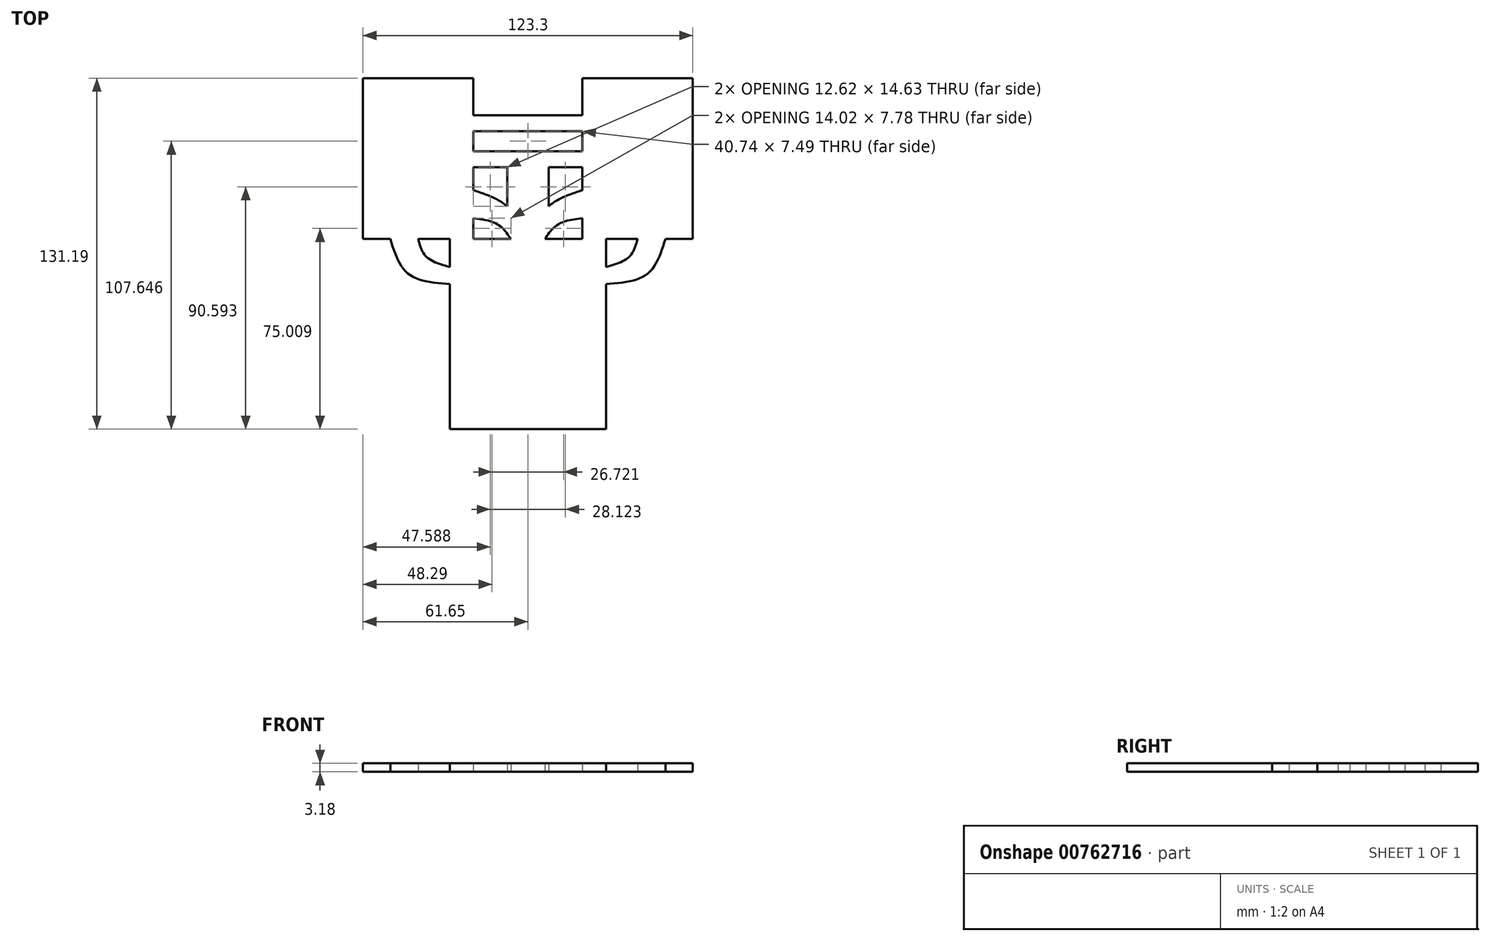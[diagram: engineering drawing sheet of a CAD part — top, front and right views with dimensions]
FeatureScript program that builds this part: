
annotation { "Feature Type Name" : "Feature", "Feature Type Description" : "" }
export const myFeature = defineFeature(function(context is Context, id is Id, definition is map)
    precondition{}
    {
        {
            var Q0;
            Q0=qCreatedBy(makeId("Top.planeOp"),FACE);
            var sketch = newSketch(context, id + "F0", { "sketchPlane" : qUnion([Q0])});
            skLineSegment(sketch, "E0", {"start": v(0, 2.42) * mm, "end": v(29.21, 2.42) * mm});
            skLineSegment(sketch, "E1", {"start": v(0, 2.42) * mm, "end": v(-29.21, 2.42) * mm});
            skLineSegment(sketch, "E2", {"start": v(-29.21, 2.42) * mm, "end": v(-29.21, -68.7) * mm});
            skLineSegment(sketch, "E3", {"start": v(29.21, 2.42) * mm, "end": v(29.21, -68.7) * mm});
            skLineSegment(sketch, "E4", {"start": v(-29.21, -68.7) * mm, "end": v(29.21, -68.7) * mm});
            skLineSegment(sketch, "E5", {"start": v(0, 2.42) * mm, "end": v(6.35, 2.42) * mm});
            skLineSegment(sketch, "E6", {"start": v(0, 2.42) * mm, "end": v(-22.91, 2.42) * mm});
            skLineSegment(sketch, "E7", {"start": v(0, 2.42) * mm, "end": v(-6.35, 2.42) * mm});
            skLineSegment(sketch, "E8", {"start": v(0, 2.42) * mm, "end": v(20.37, 2.42) * mm});
            skFitSpline(sketch, "E9", {"points": [v(6.35, 2.42) * mm, v(11.28, 7.84) * mm, v(20.37, 10.2) * mm], "startDerivative": vector(8.97, 13.22) * mm, "endDerivative": vector(18.87, 2.55) * mm});
            skFitSpline(sketch, "E10", {"points": [v(0, 2.42) * mm, v(7.75, 14.58) * mm, v(20.37, 20.64) * mm], "startDerivative": vector(12.87, 27.14) * mm, "endDerivative": vector(27.91, 9.26) * mm});
            skLineSegment(sketch, "E11", {"start": v(20.37, 2.42) * mm, "end": v(20.37, 62.5) * mm});
            skLineSegment(sketch, "E12", {"start": v(20.37, 62.5) * mm, "end": v(61.65, 62.5) * mm});
            skLineSegment(sketch, "E13", {"start": v(61.65, 62.5) * mm, "end": v(61.65, 2.42) * mm});
            skLineSegment(sketch, "E14", {"start": v(61.65, 2.42) * mm, "end": v(20.37, 2.42) * mm});
            skPoint(sketch, "E15", {"position": v(29.2, -8.05) * mm});
            skLineSegment(sketch, "E16", {"start": v(29.21, -8.05) * mm, "end": v(29.21, -14.4) * mm});
            skFitSpline(sketch, "E17", {"points": [v(29.2, -8.05) * mm, v(37.9, -4.3) * mm, v(41, 2.42) * mm], "startDerivative": vector(18.96, 5.16) * mm, "endDerivative": vector(4.34, 16) * mm});
            skLineSegment(sketch, "E18", {"start": v(41, 2.42) * mm, "end": v(51.45, 2.42) * mm});
            skFitSpline(sketch, "E19", {"points": [v(29.2, -14.4) * mm, v(44.64, -10.7) * mm, v(51.45, 2.42) * mm], "startDerivative": vector(34.5, 2.34) * mm, "endDerivative": vector(9.83, 31.47) * mm});
            skFitSpline(sketch, "E20.MirrorCS", {"points": [v(0, 2.42) * mm, v(-7.75, 14.58) * mm, v(-20.37, 20.64) * mm], "startDerivative": vector(-12.87, 27.14) * mm, "endDerivative": vector(-27.91, 9.26) * mm});
            skFitSpline(sketch, "E21.MirrorCS", {"points": [v(-6.35, 2.42) * mm, v(-11.28, 7.84) * mm, v(-20.37, 10.2) * mm], "startDerivative": vector(-8.97, 13.22) * mm, "endDerivative": vector(-18.87, 2.55) * mm});
            skFitSpline(sketch, "E22.MirrorCS", {"points": [v(-29.2, -8.05) * mm, v(-37.9, -4.3) * mm, v(-41, 2.42) * mm], "startDerivative": vector(-18.96, 5.16) * mm, "endDerivative": vector(-4.34, 16) * mm});
            skFitSpline(sketch, "E23.MirrorCS", {"points": [v(-29.2, -14.4) * mm, v(-44.64, -10.7) * mm, v(-51.45, 2.42) * mm], "startDerivative": vector(-34.5, 2.34) * mm, "endDerivative": vector(-9.83, 31.47) * mm});
            skLineSegment(sketch, "E24.MirrorCS", {"start": v(-20.37, 2.42) * mm, "end": v(-20.37, 62.5) * mm});
            skLineSegment(sketch, "E25.MirrorCS", {"start": v(-20.37, 62.5) * mm, "end": v(-61.65, 62.5) * mm});
            skLineSegment(sketch, "E26.MirrorCS", {"start": v(-61.65, 62.5) * mm, "end": v(-61.65, 2.42) * mm});
            skLineSegment(sketch, "E27.MirrorCS", {"start": v(-61.65, 2.42) * mm, "end": v(-20.37, 2.42) * mm});
            skLineSegment(sketch, "E28", {"start": v(-20.37, 42.69) * mm, "end": v(20.37, 42.69) * mm});
            skLineSegment(sketch, "E29", {"start": v(-20.37, 48.68) * mm, "end": v(20.37, 48.68) * mm});
            skLineSegment(sketch, "E30", {"start": v(-20.37, 35.2) * mm, "end": v(20.37, 35.2) * mm});
            skPoint(sketch, "E30.endSnap0", {"position": v(20.37, 32.46) * mm});
            skLineSegment(sketch, "E31", {"start": v(-20.37, 35.2) * mm, "end": v(-20.37, 29.2) * mm});
            skLineSegment(sketch, "E32", {"start": v(-20.37, 29.2) * mm, "end": v(20.37, 29.2) * mm});
            skLineSegment(sketch, "E33", {"start": v(20.37, 35.2) * mm, "end": v(20.37, 29.2) * mm});
            skLineSegment(sketch, "E34", {"start": v(-7.75, 14.58) * mm, "end": v(-7.75, 29.2) * mm});
            skLineSegment(sketch, "E35", {"start": v(7.75, 14.58) * mm, "end": v(7.75, 29.2) * mm});
            skSolve(sketch);
        }
        {
            var Q0;
            Q0 = qSketchRegion(id + "F0", true);
            var Q1;
            Q1=makeQuery(id+"F0.imprint","IMPRINT",FACE,{"disambiguationData":[TD([[makeQuery(id+"F0.imprint","IMPRINT",EDGE,{"derivedFrom":sQuery(id+"F0.wireOp",EDGE,"E7")}),-1.0]])]});
            var Q2;
            {var subQ2=sQuery(id+"F0.wireOp",EDGE,"E9");Q2=makeQuery(id+"F0.imprint","IMPRINT",FACE,{"disambiguationData":[TD([[makeQuery(id+"F0.imprint","IMPRINT",EDGE,{"derivedFrom":subQ2}),1.0]])]});}
            var Q3;
            {var subQ5=sQuery(id+"F0.wireOp",EDGE,"E21.MirrorCS");Q3=makeQuery(id+"F0.imprint","IMPRINT",FACE,{"disambiguationData":[TD([[makeQuery(id+"F0.imprint","IMPRINT",EDGE,{"derivedFrom":subQ5}),-1.0]])]});}
            var Q4;
            {var subQ0=sQuery(id+"F0.wireOp",EDGE,"E10");var subQ3=sQuery(id+"F0.wireOp",EDGE,"v0FVMibW-1Cc5-MTt6-yQMh-B5QqNteb2t81");var subQ5=makeQuery(id+"F0.imprint","INTERSECT",VERTEX,{"derivedFrom":[subQ0,subQ3]});Q4=makeQuery(id+"F0.imprint","IMPRINT",FACE,{"disambiguationData":[TD([[makeQuery(id+"F0.imprint","IMPRINT",EDGE,{"disambiguationData":[TD([[subQ5,1.0]])],"derivedFrom":subQ3}),1.0]])]});}
            var Q5;
            {var subQ0=sQuery(id+"F0.wireOp",EDGE,"E34");Q5=makeQuery(id+"F0.imprint","IMPRINT",FACE,{"disambiguationData":[TD([[makeQuery(id+"F0.imprint","IMPRINT",EDGE,{"derivedFrom":subQ0}),-1.0]])]});}
            var Q6;
            Q6=makeQuery(id+"F0.imprint","IMPRINT",FACE,{"disambiguationData":[TD([[makeQuery(id+"F0.imprint","IMPRINT",EDGE,{"derivedFrom":sQuery(id+"F0.wireOp",EDGE,"E30")}),-1.0]])]});
            extrude(context, id + "F1", {"entities" : qUnion([Q0, Q1, Q2, Q3, Q4, Q5, Q6]), "depth" : 3.17 * mm, "offsetDistance" : 25.4 * mm});
        }
    });
